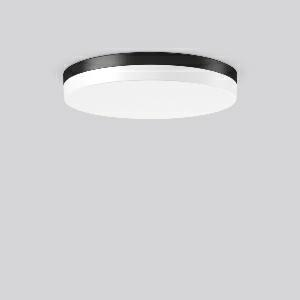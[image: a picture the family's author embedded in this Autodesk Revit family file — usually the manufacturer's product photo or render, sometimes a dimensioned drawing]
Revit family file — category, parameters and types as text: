
# Revit family: flat_slim_round_312634_0031_d3ca
name_source: partatom
category: Lighting Fixtures
units: mm (PartAtom-declared; Revit-internal decimal feet)

## family parameters
Cut with Voids When Loaded = No
Host = Face
Light Source = No
Part Type = Normal
Room Calculation Point = No
Round Connector Dimension = Use Diameter
Shared = No

## types (1)
- MultiLumen 1 830 (1 x LED Modul 830, 3450 lm, 3000)
    Apparent Load = 26 VA
    CIE Flux Codes = 40 71 90 84 100
    Color Rendering = 80
    Color Temperature = 3000
    Default Elevation = 1800 mm
    Height = 70 mm
    Lamp = 1 x LED Modul 830
    Lamp Light Flux = 3450 lm
    Lamp count = 1
    Length = 480 mm
    Lifetime = 50000 h
    Luminous efficacy = 133 lm/W
    Manufacturer = RZB
    ModVariant = No
    Model = 312634.0031
    Mounting Place = Ceiling
    Mounting Type = Surface mounted
    Number of Poles = 1
    OnlyDefault = Yes
    Power Factor = 1
    Product Name = FLAT SLIM round
    Product group = Surface mounted ceiling and wall luminaires
    ProductGroupID = 305
    Protection Class = Protection class I
    Protection Degree = Degree of protection
    RLX_Detail_Level = 1
    RLX_Emergency_Light_Flux = 0 lm
    RLX_Emergency_Type = 0
    RLX_Emergency_Type_DB = No
    RlxData = <blob elided: 23165 chars, md5=7f5ea587>
    Socket = socket
    Standby Power = 0 W
    System Light Flux = 3450 lm
    System Power = 26 W
    Type Comments = MultiLumen 1 830
    Type Image = 312633.0031.jpg
    URL = http://relux.com
    VarID = multilumen_1_830
    Voltage = 0 V
    Weight = 0.00 kg
    Width = 0 mm  [stored 0 ft]

note: [stored X ft] marks values corroborated as IEEE doubles in the binary element streams (Revit-internal decimal feet)

## geometry (parser evidence)
native form markers: Blend x4, Sweep x13
no freeform markers — native parametric forms only
